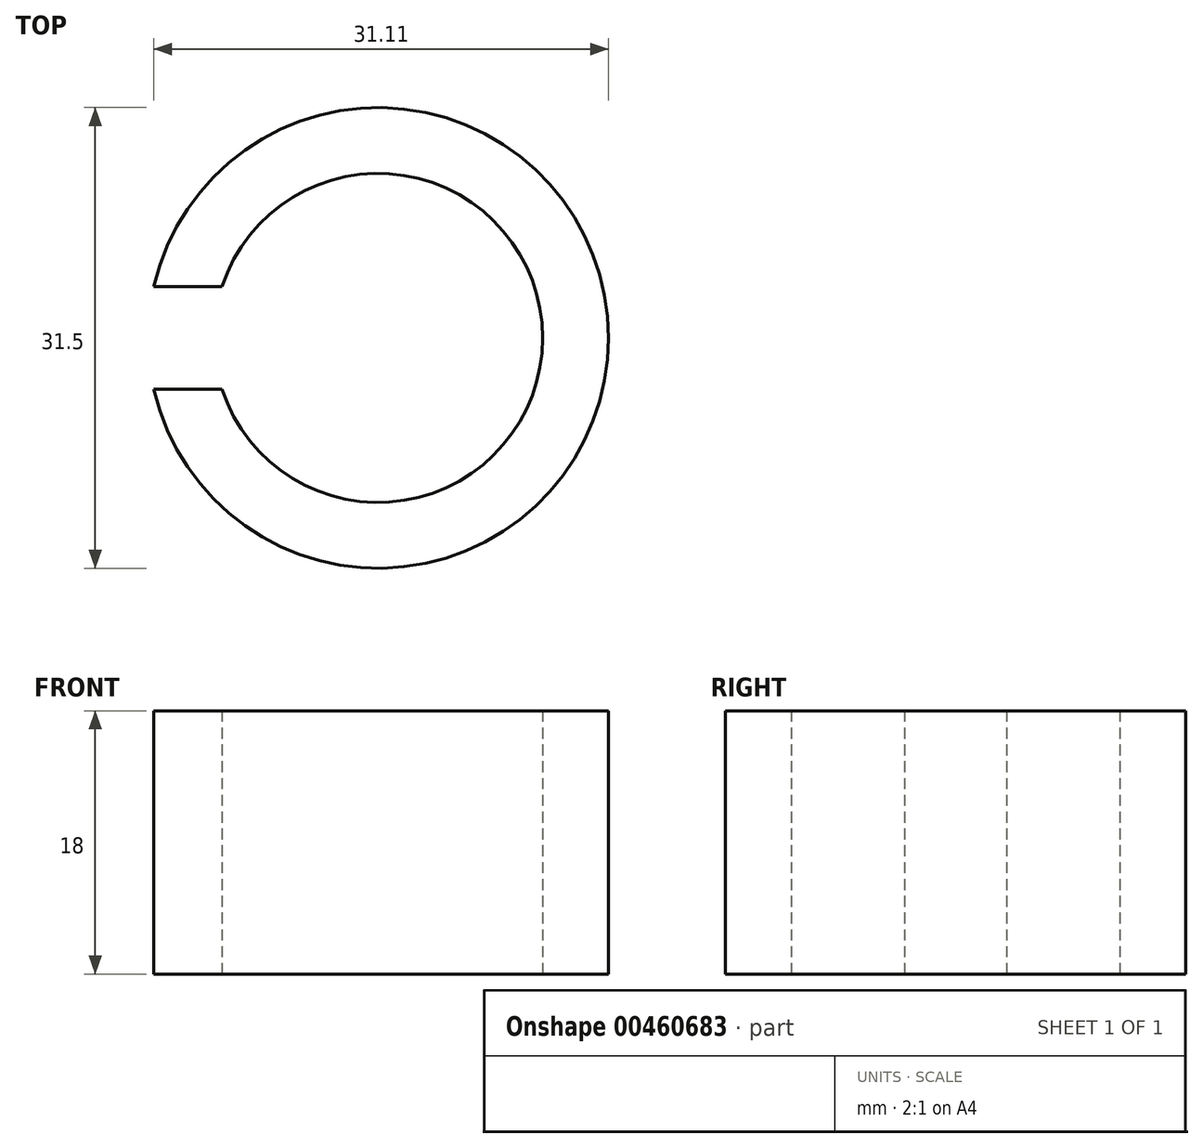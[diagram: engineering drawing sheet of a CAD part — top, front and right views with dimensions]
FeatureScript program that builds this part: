
annotation { "Feature Type Name" : "Feature", "Feature Type Description" : "" }
export const myFeature = defineFeature(function(context is Context, id is Id, definition is map)
    precondition{}
    {
        {
            var Q0;
            Q0=qCreatedBy(makeId("Top.planeOp"),FACE);
            var sketch = newSketch(context, id + "F0", { "sketchPlane" : qUnion([Q0])});
            skCircle(sketch, "E0", {"center": v(0, 0) * mm, "radius": 11.25 * mm});
            skCircle(sketch, "E1", {"center": v(0, 0) * mm, "radius": 15.75 * mm});
            skLineSegment(sketch, "E2", {"start": v(21.17, 0) * mm, "end": v(-23.46, 0) * mm, "construction": true});
            skLineSegment(sketch, "E3.bottom", {"start": v(-8.3, 3.5) * mm, "end": v(-17.88, 3.5) * mm});
            skLineSegment(sketch, "E3.top", {"start": v(-8.3, -3.5) * mm, "end": v(-17.88, -3.5) * mm});
            skLineSegment(sketch, "E3.left", {"start": v(-8.3, 3.5) * mm, "end": v(-8.3, -3.5) * mm});
            skLineSegment(sketch, "E3.right", {"start": v(-17.88, 3.5) * mm, "end": v(-17.88, -3.5) * mm});
            skSolve(sketch);
        }
        {
            var Q0;
            {var subQ0=sQuery(id+"F0.wireOp",EDGE,"E3.bottom");var subQ1=sQuery(id+"F0.wireOp",EDGE,"E0");var subQ2=makeQuery(id+"F0.imprint","INTERSECT",VERTEX,{"derivedFrom":[subQ1,subQ0]});Q0=makeQuery(id+"F0.imprint","IMPRINT",FACE,{"disambiguationData":[TD([[makeQuery(id+"F0.imprint","IMPRINT",EDGE,{"disambiguationData":[TD([[subQ2,1.0]])],"derivedFrom":subQ1}),-1.0]])]});}
            extrude(context, id + "F1", {"entities" : qUnion([Q0]), "depth" : 18 * mm, "offsetDistance" : 25 * mm});
        }
    });
